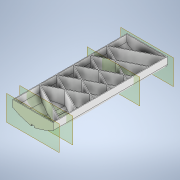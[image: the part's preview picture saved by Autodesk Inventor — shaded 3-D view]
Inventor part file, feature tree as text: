
AUTODESK INVENTOR PART (.ipt)
format: ipt  version: 2020.3 (Build 243373000, 373)  size: 778,752 bytes
history: native  units: mm
features: sketch x5, plane x4, loft x1, shell x1, rib x1, pattern_linear x1
ambient origin geometry x8: Origin, YZ Plane, XZ Plane, XY Plane, X Axis, Y Axis, Z Axis, Center Point
bodies: Solid1 (feature_tree)
feature tree (13):
  sketch  "Sketch1"  dims[d0=15.0mm d1=2.0mm d2=12.0mm]
  plane  "Work Plane4"
  loft  "Loft1"
  shell  "Shell1"  Thickness=12.0mm
  rib  "Rib1"
  pattern_linear  "Rectangular Pattern1"  Spacing1=6.0mm  [1 undecoded]
  plane  "Work Plane1"
  plane  "Work Plane2"
  plane  "Work Plane3"
  sketch  "Sketch2"  dims[d3=24.0mm]
  sketch  "Sketch3"  dims[d4=9.0mm]
  sketch  "Sketch4"  dims[d5=6.0mm]
  sketch  "Sketch5"  dims[d6=24.0mm d7=6.0mm d8=12.0mm d9=9.0mm d10=60.0mm d11=10.0mm d12=-50.0mm d13=-100.0mm d14=-20.0mm d15=11.507923mm d16=2.0mm d17=6.0mm d18=6.0mm d19=9.0mm d20=9.0mm d21=12.0mm d22=12.0mm d23=24.0mm d24=24.0mm d25=10.0mm d26=2.0mm d29=0.0mm d30=90.0deg d31=0.0mm d32=90.0deg d35=10.0mm d36=90.0deg d37=0.0mm d38=90.0deg d40=5.0mm d41=20.0mm d42=20.0mm d43=5.0mm d44=1.0mm d45=65.0mm d46=1.0mm d47=10.0mm d48=0.0mm d49=0.0mm d50=1.0mm d51=1.0mm d52=50.0mm d54=25.0mm]
note: 1 required parameter value undecoded (feature->parameter linkage not recoverable at this tier; creation-order binding heuristic only, values carry confidence <= 0.55)
